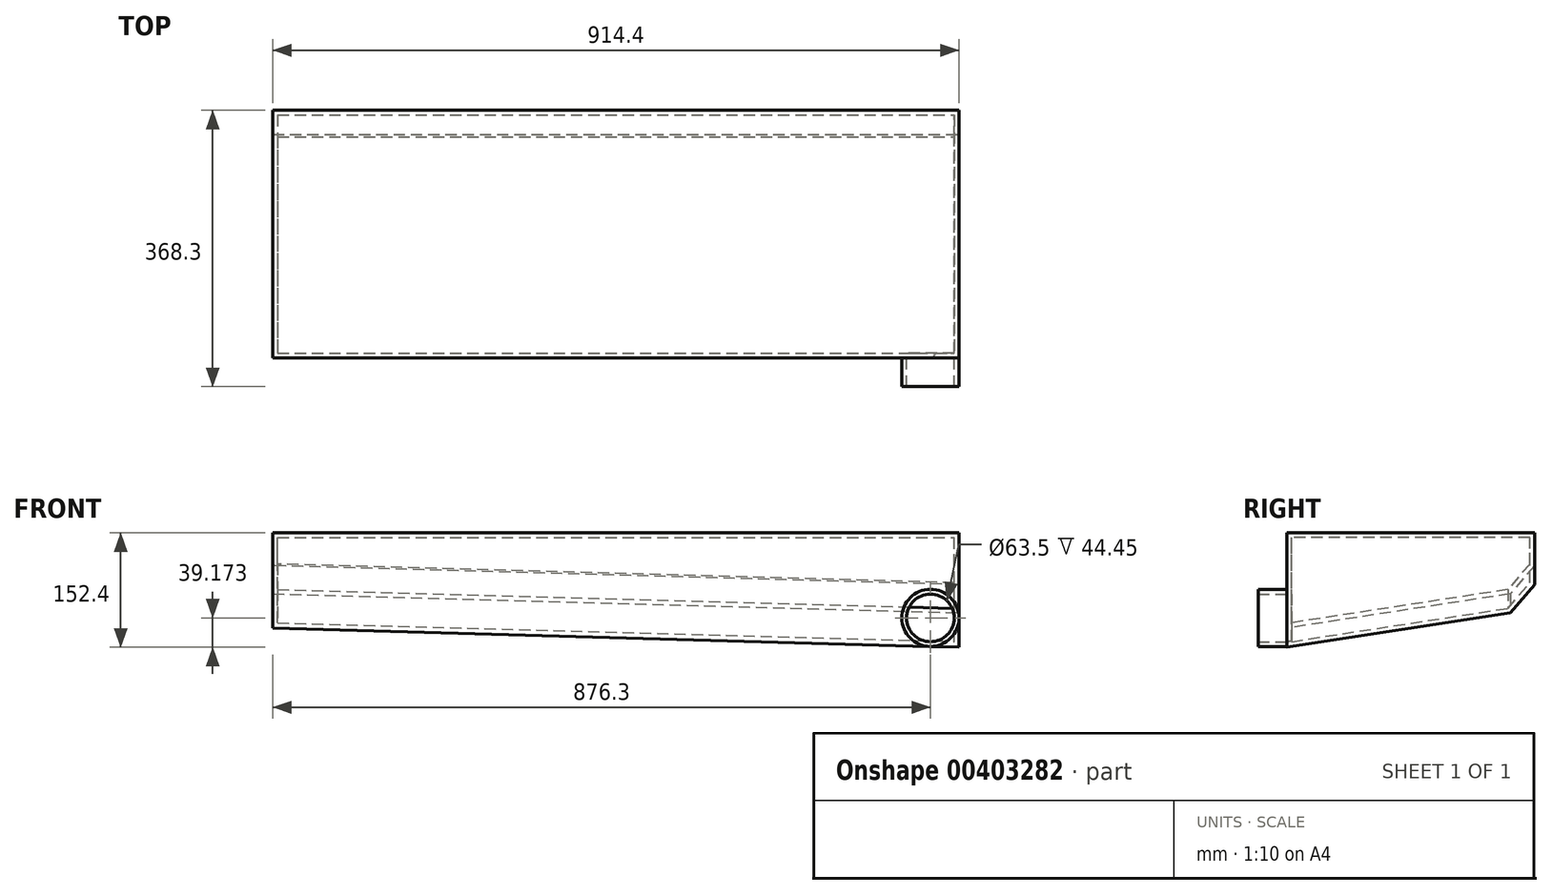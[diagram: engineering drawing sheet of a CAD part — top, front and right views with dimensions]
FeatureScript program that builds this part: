
annotation { "Feature Type Name" : "Feature", "Feature Type Description" : "" }
export const myFeature = defineFeature(function(context is Context, id is Id, definition is map)
    precondition{}
    {
        {
            var Q0;
            Q0=qCreatedBy(makeId("Top.planeOp"),FACE);
            var sketch = newSketch(context, id + "F0", { "sketchPlane" : qUnion([Q0])});
            skLineSegment(sketch, "E0.bottom", {"start": v(0, 0) * mm, "end": v(914.4, 0) * mm});
            skLineSegment(sketch, "E0.top", {"start": v(0, -330.2) * mm, "end": v(914.4, -330.2) * mm});
            skLineSegment(sketch, "E0.left", {"start": v(0, 0) * mm, "end": v(0, -330.2) * mm});
            skLineSegment(sketch, "E0.right", {"start": v(914.4, 0) * mm, "end": v(914.4, -330.2) * mm});
            skSolve(sketch);
        }
        {
            var Q0;
            Q0=qSketchRegion(id+"F0",true);
            extrude(context, id + "F1", {"entities" : qUnion([Q0]), "oppositeDirection" : true, "depth" : 152.4 * mm});
        }
        {
            var Q0;
            Q0=makeQuery(id+"F1.opExtrude","CAP_EDGE",EDGE,{"disambiguationData":[OSD([sQuery(id+"F0.wireOp",EDGE,"E0.left")])],"isStart":false});
            chamfer(context, id + "F2", {"entities" : qUnion([Q0]), "chamferType" : ChamferType.TWO_OFFSETS, "width1" : 25.4 * mm, "oppositeDirection" : false, "width2" : 914.4 * mm, "tangentPropagation" : true});
        }
        {
            var Q0;
            Q0=makeQuery(id+"F2.opChamfer","BLEND_EDGE",EDGE,{"blendedFrom":[makeQuery(id+"F1.opExtrude","CAP_EDGE",EDGE,{"disambiguationData":[OSD([sQuery(id+"F0.wireOp",EDGE,"E0.left")])],"isStart":false}),makeQuery(id+"F1.opExtrude","SWEPT_FACE",FACE,{"disambiguationData":[OSD([sQuery(id+"F0.wireOp",EDGE,"E0.bottom")])]})],"blendedInto":[makeQuery(id+"F1.opExtrude","SWEPT_FACE",FACE,{"disambiguationData":[OSD([sQuery(id+"F0.wireOp",EDGE,"E0.bottom")])]})]});
            chamfer(context, id + "F3", {"entities" : qUnion([Q0]), "chamferType" : ChamferType.TWO_OFFSETS, "width1" : 50.8 * mm, "oppositeDirection" : false, "width2" : 330.2 * mm, "tangentPropagation" : true});
        }
        {
            var Q0;
            {var subQ0=makeQuery(id+"F1.opExtrude","SWEPT_FACE",FACE,{"disambiguationData":[OSD([sQuery(id+"F0.wireOp",EDGE,"E0.bottom")])]});Q0=makeQuery(id+"F3.opChamfer","BLEND_EDGE",EDGE,{"blendedFrom":[makeQuery(id+"F2.opChamfer","BLEND_EDGE",EDGE,{"blendedFrom":[makeQuery(id+"F1.opExtrude","CAP_EDGE",EDGE,{"disambiguationData":[OSD([sQuery(id+"F0.wireOp",EDGE,"E0.left")])],"isStart":false}),subQ0],"blendedInto":[subQ0]}),subQ0],"blendedInto":[subQ0]});}
            chamfer(context, id + "F4", {"entities" : qUnion([Q0]), "width" : 38.1 * mm, "tangentPropagation" : true});
        }
        {
            var Q0;
            Q0=makeQuery(id+"F1.opExtrude","SWEPT_FACE",FACE,{"disambiguationData":[OSD([sQuery(id+"F0.wireOp",EDGE,"E0.top")])]});
            var sketch = newSketch(context, id + "F5", { "sketchPlane" : qUnion([Q0])});
            skCircle(sketch, "E1", {"center": v(876.3, -113.23) * mm, "radius": 38.1 * mm});
            skSolve(sketch);
        }
        {
            var Q0;
            Q0=qSketchRegion(id+"F5",true);
            extrude(context, id + "F6", {"entities" : qUnion([Q0]), "operationType" : NewBodyOperationType.ADD, "depth" : 38.1 * mm});
        }
        {
            var Q0;
            Q0=makeQuery(id+"F6.opExtrude","CAP_FACE",FACE,{"disambiguationData":[OSD([sQuery(id+"F5.wireOp",EDGE,"E1")])],"isStart":false});
            shell(context, id + "F7", {"entities" : qUnion([Q0]), "thickness" : 6.35 * mm});
        }
    });
